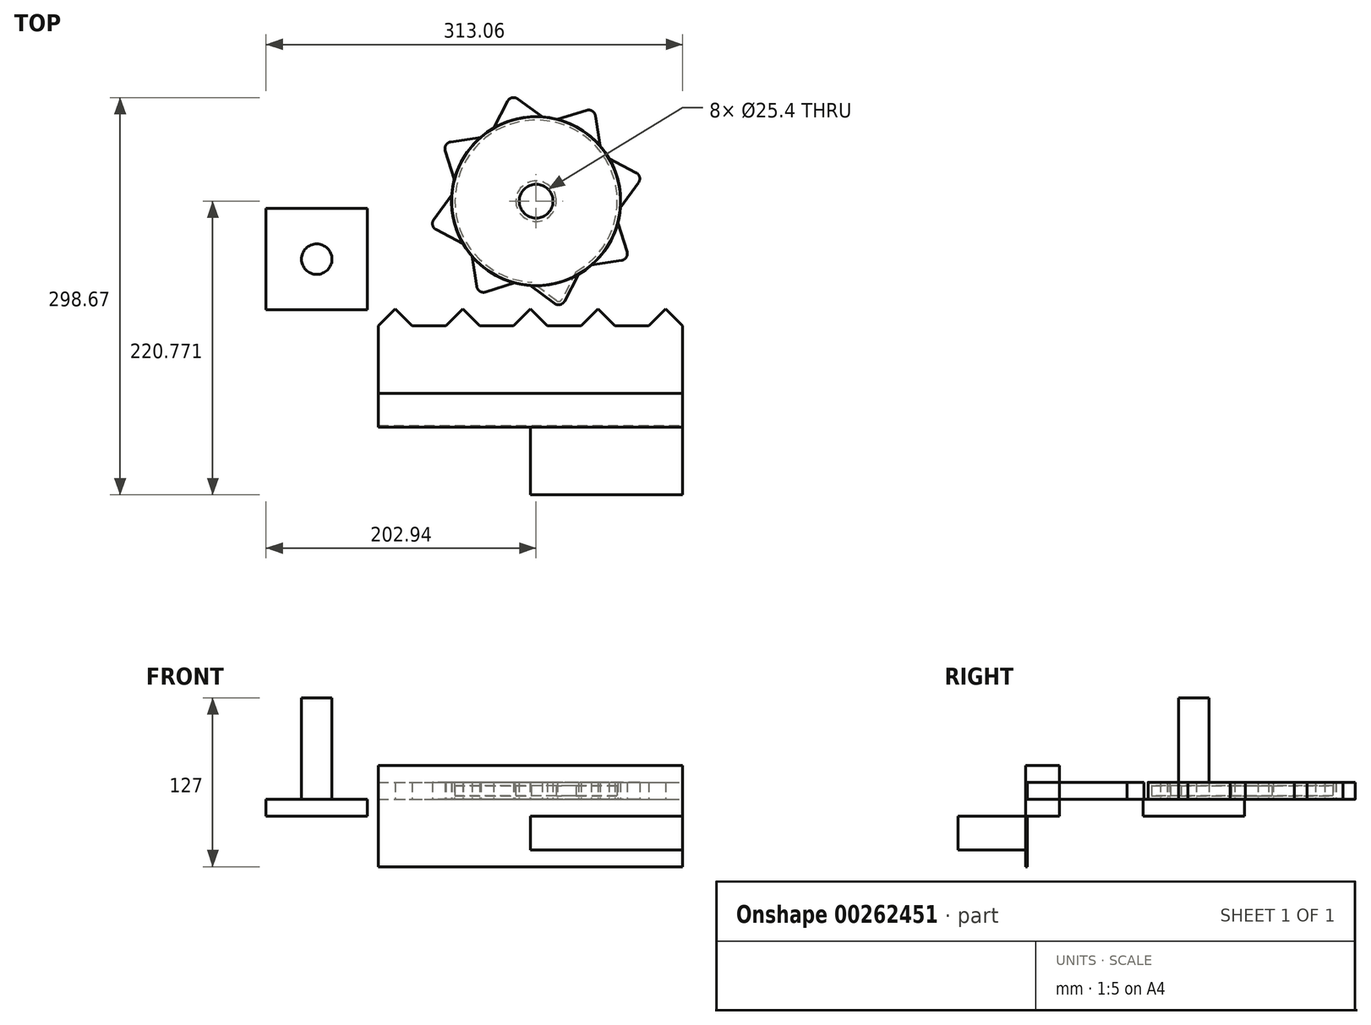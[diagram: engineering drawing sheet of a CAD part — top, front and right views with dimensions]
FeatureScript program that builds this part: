
annotation { "Feature Type Name" : "Feature", "Feature Type Description" : "" }
export const myFeature = defineFeature(function(context is Context, id is Id, definition is map)
    precondition{}
    {
        {
            var Q0;
            Q0=qCreatedBy(makeId("Top.planeOp"),FACE);
            var sketch = newSketch(context, id + "F0", { "sketchPlane" : qUnion([Q0])});
            skLineSegment(sketch, "E0.top", {"start": v(-118.48, -27.93) * mm, "end": v(110.12, -27.93) * mm});
            skLineSegment(sketch, "E0.left", {"start": v(-118.48, 22.87) * mm, "end": v(-118.48, -27.93) * mm});
            skLineSegment(sketch, "E0.right", {"start": v(110.12, 22.87) * mm, "end": v(110.12, -27.93) * mm});
            skArc(sketch, "E1", {"start": v(-93.08, 22.87) * mm, "mid": v(-105.78, 35.57) * mm, "end": v(-118.48, 22.87) * mm});
            skArc(sketch, "E2", {"start": v(-42.28, 22.87) * mm, "mid": v(-54.98, 35.57) * mm, "end": v(-67.68, 22.87) * mm});
            skArc(sketch, "E3", {"start": v(8.52, 22.87) * mm, "mid": v(-4.18, 35.57) * mm, "end": v(-16.88, 22.87) * mm});
            skLineSegment(sketch, "E4.trimOffspring", {"start": v(-42.28, 22.87) * mm, "end": v(-16.88, 22.87) * mm});
            skLineSegment(sketch, "E5.trimOffspring", {"start": v(8.52, 22.87) * mm, "end": v(33.92, 22.87) * mm});
            skLineSegment(sketch, "E6.trimOffspring", {"start": v(-93.08, 22.87) * mm, "end": v(-67.68, 22.87) * mm});
            skArc(sketch, "E7", {"start": v(59.32, 22.87) * mm, "mid": v(46.62, 35.57) * mm, "end": v(33.92, 22.87) * mm});
            skLineSegment(sketch, "E8.trimOffspring", {"start": v(59.32, 22.87) * mm, "end": v(84.72, 22.87) * mm});
            skArc(sketch, "E9", {"start": v(110.12, 22.87) * mm, "mid": v(97.42, 35.57) * mm, "end": v(84.72, 22.87) * mm});
            skLineSegment(sketch, "E10", {"start": v(-118.48, 22.87) * mm, "end": v(-105.78, 35.57) * mm});
            skLineSegment(sketch, "E11", {"start": v(-105.78, 35.57) * mm, "end": v(-93.08, 22.87) * mm});
            skLineSegment(sketch, "E12", {"start": v(-67.68, 22.87) * mm, "end": v(-54.98, 35.57) * mm});
            skLineSegment(sketch, "E13", {"start": v(-54.98, 35.57) * mm, "end": v(-42.28, 22.87) * mm});
            skLineSegment(sketch, "E14", {"start": v(-16.88, 22.87) * mm, "end": v(-4.18, 35.57) * mm});
            skLineSegment(sketch, "E15", {"start": v(-4.18, 35.57) * mm, "end": v(8.52, 22.87) * mm});
            skLineSegment(sketch, "E16", {"start": v(33.92, 22.87) * mm, "end": v(46.62, 35.57) * mm});
            skLineSegment(sketch, "E17", {"start": v(46.62, 35.57) * mm, "end": v(59.32, 22.87) * mm});
            skLineSegment(sketch, "E18", {"start": v(84.72, 22.87) * mm, "end": v(97.42, 35.57) * mm});
            skLineSegment(sketch, "E19", {"start": v(97.42, 35.57) * mm, "end": v(110.12, 22.87) * mm});
            skSolve(sketch);
        }
        {
            var Q0;
            Q0=makeQuery(id+"F0.imprint","IMPRINT",FACE,{"disambiguationData":[TD([[makeQuery(id+"F0.imprint","IMPRINT",EDGE,{"derivedFrom":sQuery(id+"F0.wireOp",EDGE,"E0.top")}),1.0]])]});
            extrude(context, id + "F1", {"entities" : qUnion([Q0]), "depth" : 12.7 * mm});
        }
        {
            var Q0;
            Q0=qCreatedBy(makeId("Top.planeOp"),FACE);
            var sketch = newSketch(context, id + "F2", { "sketchPlane" : qUnion([Q0])});
            skCircle(sketch, "E20", {"center": v(0, 116.64) * mm, "radius": 63.5 * mm});
            skCircle(sketch, "E21.cCircle", {"center": v(14.35, 54.78) * mm, "radius": 19.05 * mm, "construction": true});
            skLineSegment(sketch, "E21.0", {"start": v(32.05, 61.82) * mm, "end": v(18.66, 36.23) * mm});
            skLineSegment(sketch, "E21.1", {"start": v(18.66, 36.23) * mm, "end": v(-4.64, 53.31) * mm});
            skLineSegment(sketch, "E21.2", {"start": v(-4.64, 53.31) * mm, "end": v(32.05, 61.82) * mm});
            skCircle(sketch, "E22", {"center": v(0, 116.64) * mm, "radius": 12.7 * mm});
            skSolve(sketch);
        }
        {
            var Q0;
            {var subQ0=sQuery(id+"F2.wireOp",EDGE,"E21.2");Q0=makeQuery(id+"F2.imprint","IMPRINT",FACE,{"disambiguationData":[TD([[makeQuery(id+"F2.imprint","IMPRINT",EDGE,{"derivedFrom":subQ0}),1.0]])]});}
            var Q1;
            {var subQ1=sQuery(id+"F2.wireOp",EDGE,"E21.0");Q1=makeQuery(id+"F2.imprint","IMPRINT",FACE,{"disambiguationData":[TD([[makeQuery(id+"F2.imprint","IMPRINT",EDGE,{"derivedFrom":subQ1}),-1.0]])]});}
            var Q2;
            {var subQ0=sQuery(id+"F2.wireOp",EDGE,"E21.2");Q2=makeQuery(id+"F2.imprint","IMPRINT",FACE,{"disambiguationData":[TD([[makeQuery(id+"F2.imprint","IMPRINT",EDGE,{"derivedFrom":subQ0}),-1.0]])]});}
            extrude(context, id + "F3", {"entities" : qUnion([Q0, Q1, Q2]), "depth" : 12.7 * mm});
        }
        {
            var Q0;
            Q0=makeQuery(id+"F3.opExtrude","SWEPT_BODY",BODY,{"disambiguationData":[OSD([sQuery(id+"F2.wireOp",EDGE,"E20"),sQuery(id+"F2.wireOp",EDGE,"E21.0"),sQuery(id+"F2.wireOp",EDGE,"E21.1")])]});
            var Q1;
            Q1=sQuery(id+"F2.wireOp",EDGE,"E20");
            circularPattern(context, id + "F4", {"operationType" : NewBodyOperationType.ADD, "entities" : qUnion([Q0]), "axis" : qUnion([Q1]), "angle" : 360 * degree, "instanceCount" : 8, "equalSpace" : true});
        }
        {
            var Q0;
            Q0=makeQuery(id+"F4.opPattern","COPY",EDGE,{"derivedFrom":makeQuery(id+"F3.opExtrude","SWEPT_EDGE",EDGE,{"disambiguationData":[OSD([sQuery(id+"F2.wireOp",EDGE,"E21.0"),sQuery(id+"F2.wireOp",EDGE,"E21.1")])]}),"instanceName":"7"});
            var Q1;
            Q1=makeQuery(id+"F4.opPattern","COPY",EDGE,{"derivedFrom":makeQuery(id+"F3.opExtrude","SWEPT_EDGE",EDGE,{"disambiguationData":[OSD([sQuery(id+"F2.wireOp",EDGE,"E21.0"),sQuery(id+"F2.wireOp",EDGE,"E21.1")])]}),"instanceName":"6"});
            var Q2;
            Q2=makeQuery(id+"F4.opPattern","COPY",EDGE,{"derivedFrom":makeQuery(id+"F3.opExtrude","SWEPT_EDGE",EDGE,{"disambiguationData":[OSD([sQuery(id+"F2.wireOp",EDGE,"E21.0"),sQuery(id+"F2.wireOp",EDGE,"E21.1")])]}),"instanceName":"5"});
            var Q3;
            Q3=makeQuery(id+"F3.opExtrude","SWEPT_EDGE",EDGE,{"disambiguationData":[OSD([sQuery(id+"F2.wireOp",EDGE,"E21.0"),sQuery(id+"F2.wireOp",EDGE,"E21.1")])]});
            var Q4;
            Q4=makeQuery(id+"F4.opPattern","COPY",EDGE,{"derivedFrom":makeQuery(id+"F3.opExtrude","SWEPT_EDGE",EDGE,{"disambiguationData":[OSD([sQuery(id+"F2.wireOp",EDGE,"E21.0"),sQuery(id+"F2.wireOp",EDGE,"E21.1")])]}),"instanceName":"1"});
            var Q5;
            Q5=makeQuery(id+"F4.opPattern","COPY",EDGE,{"derivedFrom":makeQuery(id+"F3.opExtrude","SWEPT_EDGE",EDGE,{"disambiguationData":[OSD([sQuery(id+"F2.wireOp",EDGE,"E21.0"),sQuery(id+"F2.wireOp",EDGE,"E21.1")])]}),"instanceName":"2"});
            var Q6;
            Q6=makeQuery(id+"F4.opPattern","COPY",EDGE,{"derivedFrom":makeQuery(id+"F3.opExtrude","SWEPT_EDGE",EDGE,{"disambiguationData":[OSD([sQuery(id+"F2.wireOp",EDGE,"E21.0"),sQuery(id+"F2.wireOp",EDGE,"E21.1")])]}),"instanceName":"4"});
            var Q7;
            Q7=makeQuery(id+"F4.opPattern","COPY",EDGE,{"derivedFrom":makeQuery(id+"F3.opExtrude","SWEPT_EDGE",EDGE,{"disambiguationData":[OSD([sQuery(id+"F2.wireOp",EDGE,"E21.0"),sQuery(id+"F2.wireOp",EDGE,"E21.1")])]}),"instanceName":"3"});
            fillet(context, id + "F5", {"entities" : qUnion([Q0, Q1, Q2, Q3, Q4, Q5, Q6, Q7]), "radius" : 5.08 * mm, "tangentPropagation" : true, "allowEdgeOverflow" : false});
        }
        {
            var Q0;
            Q0=qCreatedBy(makeId("Top.planeOp"),FACE);
            var sketch = newSketch(context, id + "F6", { "sketchPlane" : qUnion([Q0])});
            skCircle(sketch, "E23", {"center": v(-164.84, 73.03) * mm, "radius": 11.43 * mm});
            skSolve(sketch);
        }
        {
            var Q0;
            Q0=makeQuery(id+"F6.imprint","IMPRINT",FACE,{"disambiguationData":[TD([[makeQuery(id+"F6.imprint","IMPRINT",EDGE,{"derivedFrom":sQuery(id+"F6.wireOp",EDGE,"E23")}),1.0]])]});
            extrude(context, id + "F7", {"entities" : qUnion([Q0]), "depth" : 76.2 * mm});
        }
        {
            var Q0;
            Q0=makeQuery(id+"F7.opExtrude","CAP_FACE",FACE,{"disambiguationData":[OSD([sQuery(id+"F6.wireOp",EDGE,"E23")])],"isStart":true});
            var sketch = newSketch(context, id + "F8", { "sketchPlane" : qUnion([Q0])});
            skLineSegment(sketch, "E24.bottom", {"start": v(-202.94, -34.93) * mm, "end": v(-126.74, -34.93) * mm});
            skLineSegment(sketch, "E24.top", {"start": v(-202.94, -111.13) * mm, "end": v(-126.74, -111.13) * mm});
            skLineSegment(sketch, "E24.left", {"start": v(-202.94, -34.93) * mm, "end": v(-202.94, -111.13) * mm});
            skLineSegment(sketch, "E24.right", {"start": v(-126.74, -34.93) * mm, "end": v(-126.74, -111.13) * mm});
            skPoint(sketch, "E24.middle", {"position": v(-164.84, -73.03) * mm});
            skSolve(sketch);
        }
        {
            var Q0;
            Q0=makeQuery(id+"F8.imprint","IMPRINT",FACE,{"disambiguationData":[TD([[makeQuery(id+"F8.imprint","IMPRINT",EDGE,{"derivedFrom":sQuery(id+"F8.wireOp",EDGE,"E24.bottom")}),-1.0]])]});
            var Q1;
            Q1=makeQuery(id+"F8.imprint","IMPRINT",FACE,{"disambiguationData":[TD([[makeQuery(id+"F8.imprint","IMPRINT",EDGE,{"derivedFrom":makeQuery(id+"F7.opExtrude","CAP_EDGE",EDGE,{"disambiguationData":[OSD([sQuery(id+"F6.wireOp",EDGE,"E23")])],"isStart":true})}),-1.0]])]});
            extrude(context, id + "F9", {"entities" : qUnion([Q0, Q1]), "operationType" : NewBodyOperationType.ADD, "depth" : 12.7 * mm});
        }
        {
            var Q0;
            Q0=makeQuery(id+"F1.opExtrude","SWEPT_FACE",FACE,{"disambiguationData":[OSD([sQuery(id+"F0.wireOp",EDGE,"E0.top")])]});
            var sketch = newSketch(context, id + "F10", { "sketchPlane" : qUnion([Q0])});
            skLineSegment(sketch, "E25.bottom", {"start": v(-118.48, 12.7) * mm, "end": v(110.12, 12.7) * mm});
            skLineSegment(sketch, "E25.top", {"start": v(-118.48, 0) * mm, "end": v(110.12, 0) * mm});
            skLineSegment(sketch, "E25.left", {"start": v(-118.48, 12.7) * mm, "end": v(-118.48, 0) * mm});
            skLineSegment(sketch, "E25.right", {"start": v(110.12, 12.7) * mm, "end": v(110.12, 0) * mm});
            skLineSegment(sketch, "E26.top", {"start": v(-118.48, 25.4) * mm, "end": v(110.12, 25.4) * mm});
            skLineSegment(sketch, "E26.left", {"start": v(-118.48, 0) * mm, "end": v(-118.48, 25.4) * mm});
            skLineSegment(sketch, "E26.right", {"start": v(110.12, 0) * mm, "end": v(110.12, 25.4) * mm});
            skPoint(sketch, "E26.middle", {"position": v(-4.18, 12.7) * mm});
            skLineSegment(sketch, "E27.top", {"start": v(-118.48, -12.7) * mm, "end": v(110.12, -12.7) * mm});
            skLineSegment(sketch, "E27.left", {"start": v(-118.48, 12.7) * mm, "end": v(-118.48, -12.7) * mm});
            skLineSegment(sketch, "E27.right", {"start": v(110.12, 12.7) * mm, "end": v(110.12, -12.7) * mm});
            skPoint(sketch, "E27.middle", {"position": v(-4.18, 0) * mm});
            skLineSegment(sketch, "E28.left", {"start": v(-118.48, 25.4) * mm, "end": v(-118.48, -12.7) * mm});
            skLineSegment(sketch, "E28.right", {"start": v(110.12, 25.4) * mm, "end": v(110.12, -12.7) * mm});
            skLineSegment(sketch, "E29.left", {"start": v(-118.48, 25.4) * mm, "end": v(-118.48, 12.7) * mm});
            skLineSegment(sketch, "E29.right", {"start": v(110.12, 25.4) * mm, "end": v(110.12, 12.7) * mm});
            skLineSegment(sketch, "E30.left", {"start": v(-118.48, -12.7) * mm, "end": v(-118.48, 0) * mm});
            skLineSegment(sketch, "E30.right", {"start": v(110.12, -12.7) * mm, "end": v(110.12, 0) * mm});
            skSolve(sketch);
        }
        {
            var Q0;
            Q0=makeQuery(id+"F10.imprint","IMPRINT",FACE,{"disambiguationData":[TD([[makeQuery(id+"F10.imprint","IMPRINT",EDGE,{"derivedFrom":sQuery(id+"F10.wireOp",EDGE,"E26.top")}),-1.0]])]});
            var Q1;
            Q1=makeQuery(id+"F10.imprint","IMPRINT",FACE,{"disambiguationData":[TD([[makeQuery(id+"F10.imprint","IMPRINT",EDGE,{"derivedFrom":sQuery(id+"F10.wireOp",EDGE,"E27.top")}),1.0]])]});
            extrude(context, id + "F11", {"entities" : qUnion([Q0, Q1]), "depth" : 25.4 * mm});
        }
        {
            var Q0;
            Q0=makeQuery(id+"F11.opExtrude","CAP_FACE",FACE,{"disambiguationData":[OSD([sQuery(id+"F10.wireOp",EDGE,"E26.top"),sQuery(id+"F10.wireOp",EDGE,"E25.bottom"),sQuery(id+"F10.wireOp",EDGE,"E29.left"),sQuery(id+"F10.wireOp",EDGE,"E29.right")])],"isStart":false});
            var sketch = newSketch(context, id + "F12", { "sketchPlane" : qUnion([Q0])});
            skLineSegment(sketch, "E31.bottom", {"start": v(-118.48, 25.4) * mm, "end": v(110.12, 25.4) * mm});
            skLineSegment(sketch, "E31.top", {"start": v(-118.48, -50.8) * mm, "end": v(110.12, -50.8) * mm});
            skLineSegment(sketch, "E31.left", {"start": v(-118.48, 25.4) * mm, "end": v(-118.48, -50.8) * mm});
            skLineSegment(sketch, "E31.right", {"start": v(110.12, 25.4) * mm, "end": v(110.12, -50.8) * mm});
            skSolve(sketch);
        }
        {
            var Q0;
            Q0 = qSketchRegion(id + "F12", true);
            extrude(context, id + "F13", {"entities" : qUnion([Q0]), "operationType" : NewBodyOperationType.ADD, "oppositeDirection" : true, "depth" : 1.27 * mm});
        }
        {
            var Q0;
            Q0=makeQuery(id+"F11.opExtrude","SWEPT_FACE",FACE,{"disambiguationData":[OSD([sQuery(id+"F10.wireOp",EDGE,"E27.top")])]});
            var sketch = newSketch(context, id + "F14", { "sketchPlane" : qUnion([Q0])});
            skLineSegment(sketch, "E32.bottom", {"start": v(-118.48, 40) * mm, "end": v(110.12, 40) * mm});
            skLineSegment(sketch, "E32.top", {"start": v(-118.48, 27.93) * mm, "end": v(110.12, 27.93) * mm});
            skLineSegment(sketch, "E32.left", {"start": v(-118.48, 40) * mm, "end": v(-118.48, 27.93) * mm});
            skLineSegment(sketch, "E32.right", {"start": v(110.12, 40) * mm, "end": v(110.12, 27.93) * mm});
            skLineSegment(sketch, "E33.bottom", {"start": v(-4.18, 40) * mm, "end": v(-118.48, 40) * mm});
            skLineSegment(sketch, "E33.top", {"start": v(-4.18, 52.7) * mm, "end": v(-118.48, 52.7) * mm});
            skLineSegment(sketch, "E33.left", {"start": v(-4.18, 40) * mm, "end": v(-4.18, 52.7) * mm});
            skLineSegment(sketch, "E33.right", {"start": v(-118.48, 40) * mm, "end": v(-118.48, 52.7) * mm});
            skLineSegment(sketch, "E34.bottom", {"start": v(-4.18, 40) * mm, "end": v(110.12, 40) * mm});
            skLineSegment(sketch, "E34.top", {"start": v(-4.18, 104.13) * mm, "end": v(110.12, 104.13) * mm});
            skLineSegment(sketch, "E34.left", {"start": v(-4.18, 40) * mm, "end": v(-4.18, 104.13) * mm});
            skLineSegment(sketch, "E34.right", {"start": v(110.12, 40) * mm, "end": v(110.12, 104.13) * mm});
            skLineSegment(sketch, "E35.bottom", {"start": v(-118.48, 27.93) * mm, "end": v(-4.18, 27.93) * mm});
            skLineSegment(sketch, "E35.top", {"start": v(-118.48, 40) * mm, "end": v(-4.18, 40) * mm});
            skLineSegment(sketch, "E35.left", {"start": v(-118.48, 27.93) * mm, "end": v(-118.48, 40) * mm});
            skLineSegment(sketch, "E35.right", {"start": v(-4.18, 27.93) * mm, "end": v(-4.18, 40) * mm});
            skLineSegment(sketch, "E36.top", {"start": v(-4.18, 27.93) * mm, "end": v(110.12, 27.93) * mm});
            skLineSegment(sketch, "E36.left", {"start": v(-4.18, 40) * mm, "end": v(-4.18, 27.93) * mm});
            skLineSegment(sketch, "E37.bottom", {"start": v(52.97, 27.93) * mm, "end": v(-61.33, 27.93) * mm});
            skLineSegment(sketch, "E37.top", {"start": v(52.97, 52.7) * mm, "end": v(-61.33, 52.7) * mm});
            skLineSegment(sketch, "E37.left", {"start": v(52.97, 27.93) * mm, "end": v(52.97, 52.7) * mm});
            skLineSegment(sketch, "E37.right", {"start": v(-61.33, 27.93) * mm, "end": v(-61.33, 52.7) * mm});
            skCircle(sketch, "E38", {"center": v(-61.33, 40) * mm, "radius": 12.7 * mm});
            skCircle(sketch, "E39", {"center": v(52.97, 40) * mm, "radius": 12.7 * mm});
            skSolve(sketch);
        }
        {
            var Q0;
            {var subQ0=sQuery(id+"F14.wireOp",EDGE,"E34.left");Q0=makeQuery(id+"F14.imprint","IMPRINT",FACE,{"disambiguationData":[TD([[makeQuery(id+"F14.imprint","IMPRINT",EDGE,{"derivedFrom":subQ0}),1.0]])]});}
            var Q1;
            {var subQ0=sQuery(id+"F14.wireOp",EDGE,"E36.left");Q1=makeQuery(id+"F14.imprint","IMPRINT",FACE,{"disambiguationData":[TD([[makeQuery(id+"F14.imprint","IMPRINT",EDGE,{"derivedFrom":subQ0}),-1.0]])]});}
            var Q2;
            {var subQ0=sQuery(id+"F14.wireOp",EDGE,"E36.left");Q2=makeQuery(id+"F14.imprint","IMPRINT",FACE,{"disambiguationData":[TD([[makeQuery(id+"F14.imprint","IMPRINT",EDGE,{"derivedFrom":subQ0}),1.0]])]});}
            var Q3;
            {var subQ0=sQuery(id+"F14.wireOp",EDGE,"E34.left");Q3=makeQuery(id+"F14.imprint","IMPRINT",FACE,{"disambiguationData":[TD([[makeQuery(id+"F14.imprint","IMPRINT",EDGE,{"derivedFrom":subQ0}),-1.0]])]});}
            var Q4;
            {var subQ0=sQuery(id+"F14.wireOp",EDGE,"E38");var subQ1=sQuery(id+"F14.wireOp",EDGE,"E35.top");var subQ2=makeQuery(id+"F14.imprint","INTERSECT",VERTEX,{"disambiguationData":[OD(0.0)],"derivedFrom":[subQ1,subQ0]});Q4=makeQuery(id+"F14.imprint","IMPRINT",FACE,{"disambiguationData":[TD([[makeQuery(id+"F14.imprint","IMPRINT",EDGE,{"disambiguationData":[TD([[subQ2,-1.0]])],"derivedFrom":subQ1}),1.0]])]});}
            var Q5;
            {var subQ0=sQuery(id+"F14.wireOp",EDGE,"E38");var subQ1=sQuery(id+"F14.wireOp",EDGE,"E35.top");var subQ2=makeQuery(id+"F14.imprint","INTERSECT",VERTEX,{"disambiguationData":[OD(0.0)],"derivedFrom":[subQ1,subQ0]});Q5=makeQuery(id+"F14.imprint","IMPRINT",FACE,{"disambiguationData":[TD([[makeQuery(id+"F14.imprint","IMPRINT",EDGE,{"disambiguationData":[TD([[subQ2,-1.0]])],"derivedFrom":subQ1}),-1.0]])]});}
            var Q6;
            {var subQ0=sQuery(id+"F14.wireOp",EDGE,"E37.right");var subQ1=sQuery(id+"F14.wireOp",EDGE,"E35.top");var subQ2=makeQuery(id+"F14.imprint","INTERSECT",VERTEX,{"derivedFrom":[subQ1,subQ0]});Q6=makeQuery(id+"F14.imprint","IMPRINT",FACE,{"disambiguationData":[TD([[makeQuery(id+"F14.imprint","IMPRINT",EDGE,{"disambiguationData":[TD([[subQ2,-1.0]])],"derivedFrom":subQ1}),-1.0]])]});}
            var Q7;
            {var subQ0=sQuery(id+"F14.wireOp",EDGE,"E37.right");var subQ1=sQuery(id+"F14.wireOp",EDGE,"E35.top");var subQ2=makeQuery(id+"F14.imprint","INTERSECT",VERTEX,{"derivedFrom":[subQ1,subQ0]});Q7=makeQuery(id+"F14.imprint","IMPRINT",FACE,{"disambiguationData":[TD([[makeQuery(id+"F14.imprint","IMPRINT",EDGE,{"disambiguationData":[TD([[subQ2,-1.0]])],"derivedFrom":subQ1}),1.0]])]});}
            var Q8;
            {var subQ0=sQuery(id+"F14.wireOp",EDGE,"E39");var subQ1=sQuery(id+"F14.wireOp",EDGE,"E34.bottom");var subQ2=makeQuery(id+"F14.imprint","INTERSECT",VERTEX,{"disambiguationData":[OD(0.0)],"derivedFrom":[subQ1,subQ0]});Q8=makeQuery(id+"F14.imprint","IMPRINT",FACE,{"disambiguationData":[TD([[makeQuery(id+"F14.imprint","IMPRINT",EDGE,{"disambiguationData":[TD([[subQ2,-1.0]])],"derivedFrom":subQ1}),1.0]])]});}
            var Q9;
            {var subQ0=sQuery(id+"F14.wireOp",EDGE,"E37.left");var subQ1=sQuery(id+"F14.wireOp",EDGE,"E34.bottom");var subQ2=makeQuery(id+"F14.imprint","INTERSECT",VERTEX,{"derivedFrom":[subQ1,subQ0]});Q9=makeQuery(id+"F14.imprint","IMPRINT",FACE,{"disambiguationData":[TD([[makeQuery(id+"F14.imprint","IMPRINT",EDGE,{"disambiguationData":[TD([[subQ2,-1.0]])],"derivedFrom":subQ1}),-1.0]])]});}
            var Q10;
            {var subQ0=sQuery(id+"F14.wireOp",EDGE,"E37.left");var subQ1=sQuery(id+"F14.wireOp",EDGE,"E34.bottom");var subQ2=makeQuery(id+"F14.imprint","INTERSECT",VERTEX,{"derivedFrom":[subQ1,subQ0]});Q10=makeQuery(id+"F14.imprint","IMPRINT",FACE,{"disambiguationData":[TD([[makeQuery(id+"F14.imprint","IMPRINT",EDGE,{"disambiguationData":[TD([[subQ2,-1.0]])],"derivedFrom":subQ1}),1.0]])]});}
            var Q11;
            {var subQ0=sQuery(id+"F14.wireOp",EDGE,"E39");var subQ1=sQuery(id+"F14.wireOp",EDGE,"E34.bottom");var subQ2=makeQuery(id+"F14.imprint","INTERSECT",VERTEX,{"disambiguationData":[OD(0.0)],"derivedFrom":[subQ1,subQ0]});Q11=makeQuery(id+"F14.imprint","IMPRINT",FACE,{"disambiguationData":[TD([[makeQuery(id+"F14.imprint","IMPRINT",EDGE,{"disambiguationData":[TD([[subQ2,-1.0]])],"derivedFrom":subQ1}),-1.0]])]});}
            extrude(context, id + "F15", {"entities" : qUnion([Q0, Q1, Q2, Q3, Q4, Q5, Q6, Q7, Q8, Q9, Q10, Q11]), "operationType" : NewBodyOperationType.ADD, "depth" : 0.03 * mm});
        }
        {
            var Q0;
            Q0=makeQuery(id+"F15.opExtrude","CAP_FACE",FACE,{"disambiguationData":[OSD([sQuery(id+"F14.wireOp",EDGE,"E37.bottom"),sQuery(id+"F14.wireOp",EDGE,"E37.top"),sQuery(id+"F14.wireOp",EDGE,"E38"),sQuery(id+"F14.wireOp",EDGE,"E39")])],"isStart":false});
            var sketch = newSketch(context, id + "F16", { "sketchPlane" : qUnion([Q0])});
            skCircle(sketch, "E40", {"center": v(-61.33, 40) * mm, "radius": 12.7 * mm});
            skLineSegment(sketch, "E41.bottom", {"start": v(-57.37, 53.33) * mm, "end": v(56.93, 53.33) * mm});
            skLineSegment(sketch, "E41.top", {"start": v(-57.37, 27.93) * mm, "end": v(56.93, 27.93) * mm});
            skLineSegment(sketch, "E41.left", {"start": v(-57.37, 53.33) * mm, "end": v(-57.37, 27.93) * mm});
            skLineSegment(sketch, "E41.right", {"start": v(56.93, 53.33) * mm, "end": v(56.93, 27.93) * mm});
            skCircle(sketch, "E42", {"center": v(56.93, 40.63) * mm, "radius": 12.7 * mm});
            skLineSegment(sketch, "E43.bottom", {"start": v(-120.85, 129.53) * mm, "end": v(183.95, 129.53) * mm});
            skLineSegment(sketch, "E43.top", {"start": v(-120.85, -175.27) * mm, "end": v(183.95, -175.27) * mm});
            skLineSegment(sketch, "E43.left", {"start": v(-120.85, 129.53) * mm, "end": v(-120.85, -175.27) * mm});
            skLineSegment(sketch, "E43.right", {"start": v(183.95, 129.53) * mm, "end": v(183.95, -175.27) * mm});
            skSolve(sketch);
        }
        {
            var Q0;
            {var subQ2=sQuery(id+"F16.wireOp",EDGE,"E41.bottom");Q0=makeQuery(id+"F16.imprint","IMPRINT",FACE,{"disambiguationData":[TD([[makeQuery(id+"F16.imprint","IMPRINT",EDGE,{"derivedFrom":subQ2}),1.0]])]});}
            extrude(context, id + "F17", {"entities" : qUnion([Q0]), "depth" : 25.4 * mm});
        }
        {
            var Q0;
            {var subQ0=makeQuery(id+"F3.opExtrude","CAP_FACE",FACE,{"disambiguationData":[OSD([sQuery(id+"F2.wireOp",EDGE,"E20"),sQuery(id+"F2.wireOp",EDGE,"E21.0"),sQuery(id+"F2.wireOp",EDGE,"E21.1"),sQuery(id+"F2.wireOp",EDGE,"E22")])],"isStart":false});Q0=makeQuery(id+"F4.boolean.opBoolean","MERGE",FACE,{"derivedFrom":[subQ0,makeQuery(id+"F4.opPattern","COPY",FACE,{"derivedFrom":subQ0,"instanceName":"1"}),makeQuery(id+"F4.opPattern","COPY",FACE,{"derivedFrom":subQ0,"instanceName":"2"}),makeQuery(id+"F4.opPattern","COPY",FACE,{"derivedFrom":subQ0,"instanceName":"3"}),makeQuery(id+"F4.opPattern","COPY",FACE,{"derivedFrom":subQ0,"instanceName":"4"}),makeQuery(id+"F4.opPattern","COPY",FACE,{"derivedFrom":subQ0,"instanceName":"5"}),makeQuery(id+"F4.opPattern","COPY",FACE,{"derivedFrom":subQ0,"instanceName":"6"}),makeQuery(id+"F4.opPattern","COPY",FACE,{"derivedFrom":subQ0,"instanceName":"7"})]});}
            var Q1;
            Q1=makeQuery(id+"F3.opExtrude","SWEPT_BODY",BODY,{"disambiguationData":[OSD([sQuery(id+"F2.wireOp",EDGE,"E20"),sQuery(id+"F2.wireOp",EDGE,"E21.0"),sQuery(id+"F2.wireOp",EDGE,"E21.1"),sQuery(id+"F2.wireOp",EDGE,"E22")])]});
            shell(context, id + "F18", {"isHollow" : true, "entities" : qUnion([Q0]), "parts" : qUnion([Q1]), "thickness" : 2.54 * mm});
        }
    });
